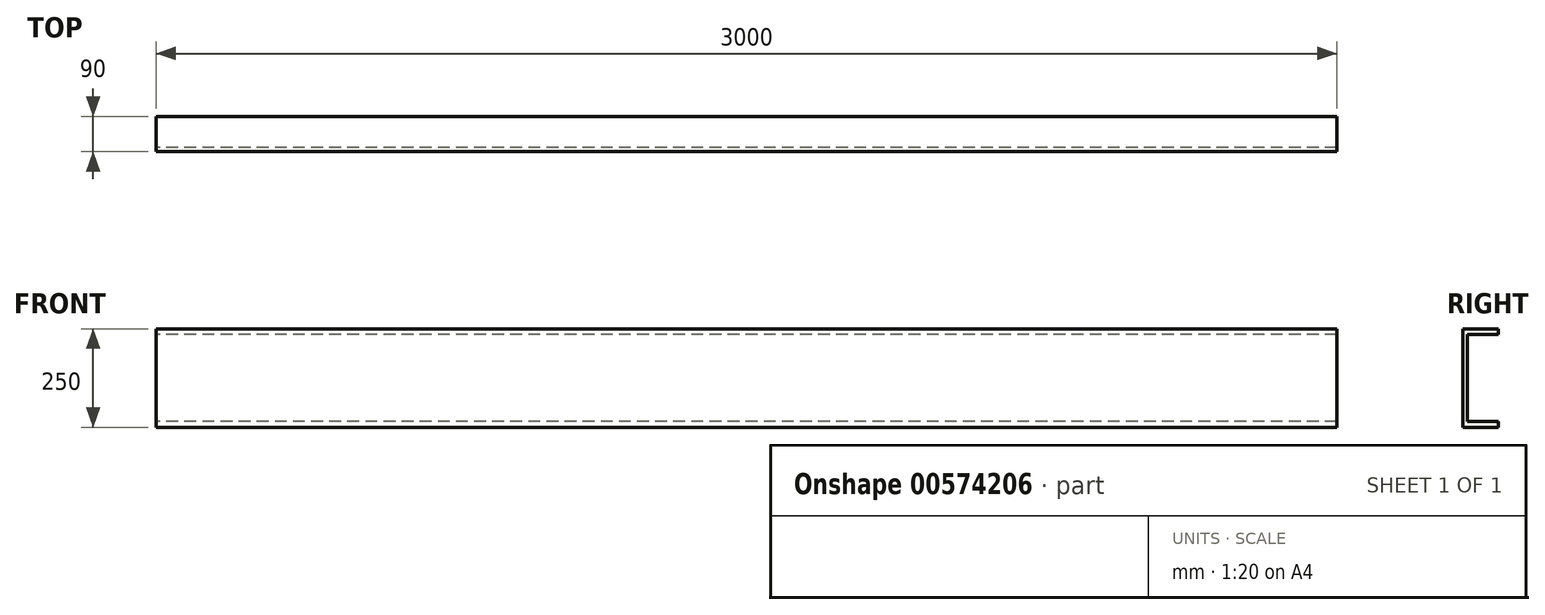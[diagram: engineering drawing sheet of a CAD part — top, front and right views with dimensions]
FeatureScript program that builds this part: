
annotation { "Feature Type Name" : "Feature", "Feature Type Description" : "" }
export const myFeature = defineFeature(function(context is Context, id is Id, definition is map)
    precondition{}
    {
        {
            var Q0;
            Q0=qCreatedBy(makeId("Right.planeOp"),FACE);
            var sketch = newSketch(context, id + "F0", { "sketchPlane" : qUnion([Q0])});
            skLineSegment(sketch, "E0", {"start": v(0, 0) * mm, "end": v(0, 250) * mm});
            skLineSegment(sketch, "E1", {"start": v(0, 250) * mm, "end": v(90, 250) * mm});
            skLineSegment(sketch, "E2", {"start": v(90, 250) * mm, "end": v(90, 235.5) * mm});
            skLineSegment(sketch, "E3", {"start": v(90, 235.5) * mm, "end": v(11, 235.5) * mm});
            skLineSegment(sketch, "E4", {"start": v(11, 235.5) * mm, "end": v(11, 14.5) * mm});
            skLineSegment(sketch, "E5", {"start": v(11, 14.5) * mm, "end": v(90, 14.5) * mm});
            skLineSegment(sketch, "E6", {"start": v(90, 14.5) * mm, "end": v(90, 0) * mm});
            skLineSegment(sketch, "E7", {"start": v(90, 0) * mm, "end": v(0, 0) * mm});
            skSolve(sketch);
        }
        {
            var Q0;
            Q0=qSketchRegion(id+"F0",true);
            extrude(context, id + "F1", {"entities" : qUnion([Q0]), "depth" : 3000 * mm, "offsetDistance" : 25 * mm});
        }
    });
